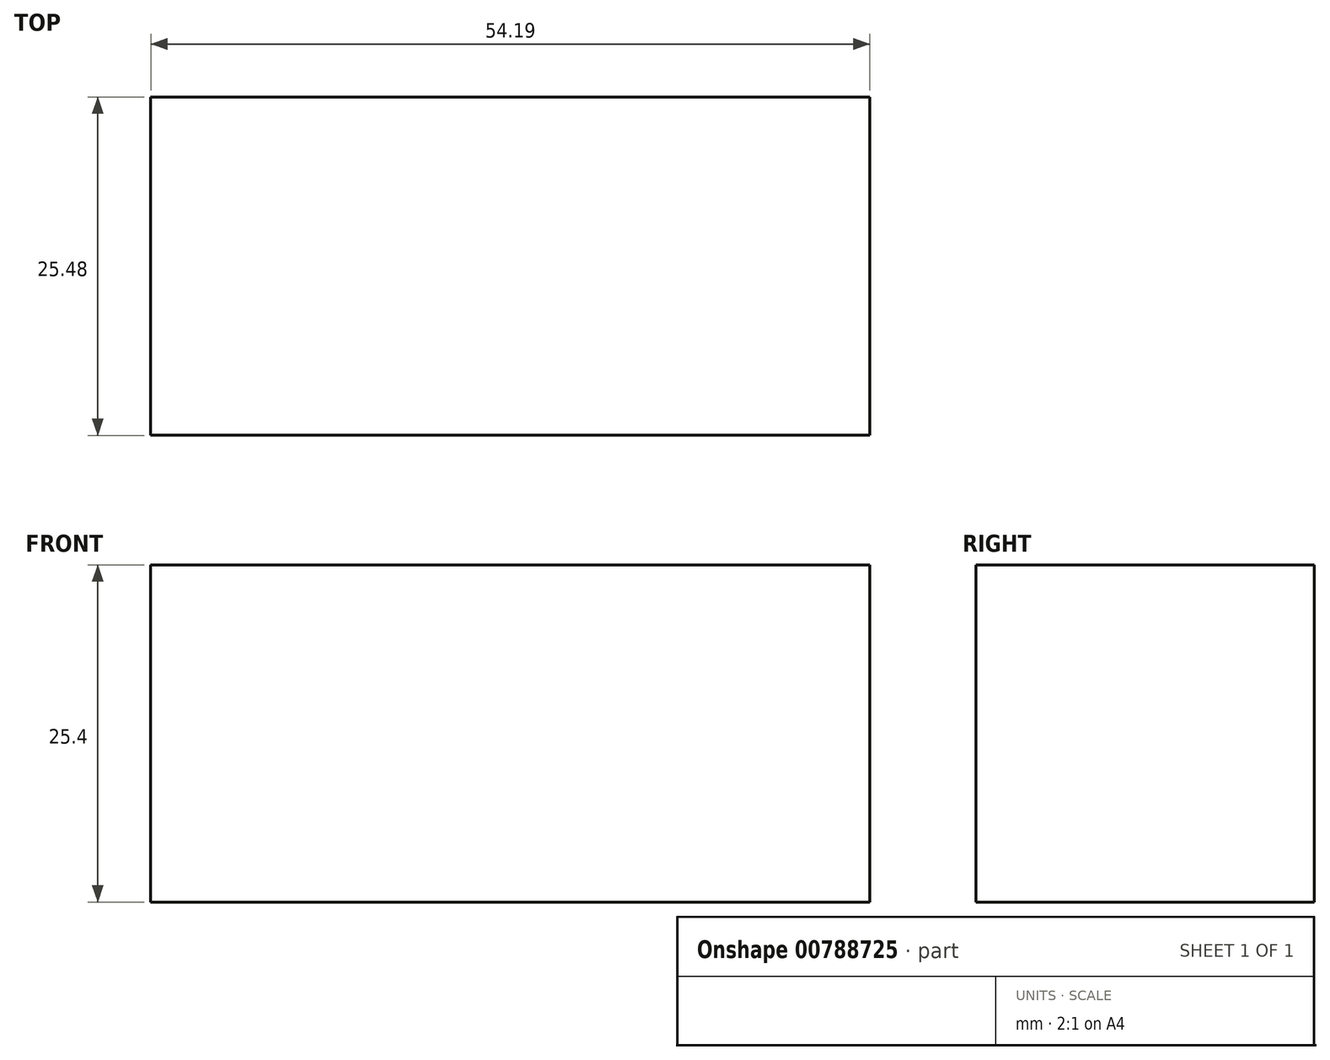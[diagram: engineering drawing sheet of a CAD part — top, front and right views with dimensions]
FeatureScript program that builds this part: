
annotation { "Feature Type Name" : "Feature", "Feature Type Description" : "" }
export const myFeature = defineFeature(function(context is Context, id is Id, definition is map)
    precondition{}
    {
        {
            var Q0;
            Q0=qCreatedBy(makeId("Top.planeOp"),FACE);
            var sketch = newSketch(context, id + "F0", { "sketchPlane" : qUnion([Q0])});
            skLineSegment(sketch, "E0.bottom", {"start": v(-26.08, 0) * mm, "end": v(28.11, 0) * mm});
            skLineSegment(sketch, "E0.top", {"start": v(-26.08, -25.48) * mm, "end": v(28.11, -25.48) * mm});
            skLineSegment(sketch, "E0.left", {"start": v(-26.08, 0) * mm, "end": v(-26.08, -25.48) * mm});
            skLineSegment(sketch, "E0.right", {"start": v(28.11, 0) * mm, "end": v(28.11, -25.48) * mm});
            skSolve(sketch);
        }
        {
            var Q0;
            Q0=makeQuery(id+"F0.imprint","IMPRINT",FACE,{"disambiguationData":[TD([[makeQuery(id+"F0.imprint","IMPRINT",EDGE,{"derivedFrom":sQuery(id+"F0.wireOp",EDGE,"E0.bottom")}),-1.0]])]});
            extrude(context, id + "F1", {"entities" : qUnion([Q0]), "depth" : 25.4 * mm, "offsetDistance" : 25.4 * mm});
        }
    });
